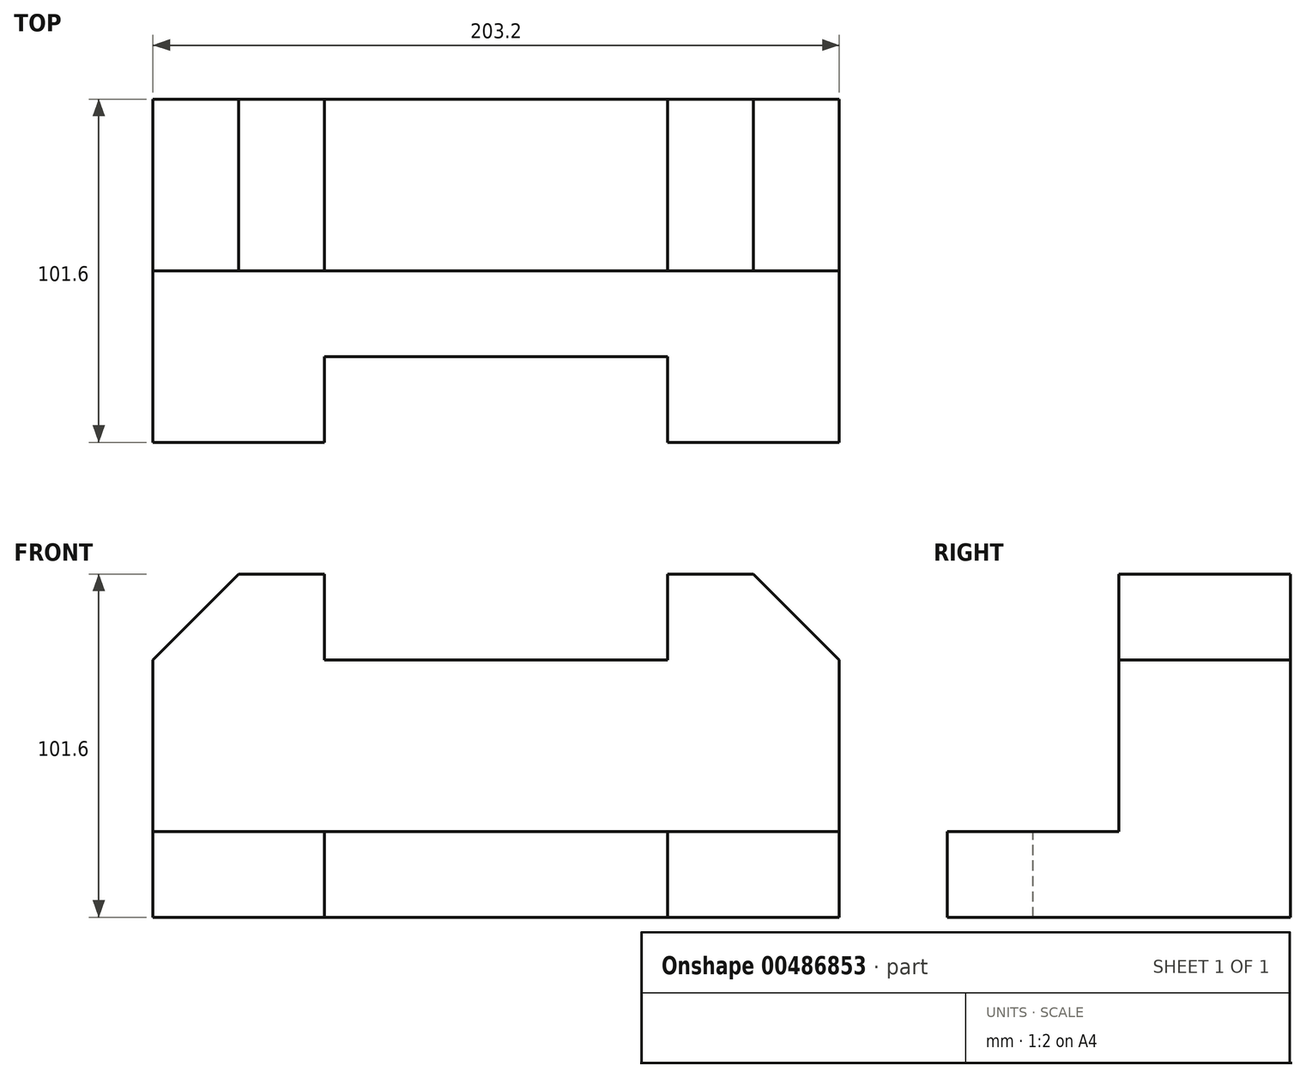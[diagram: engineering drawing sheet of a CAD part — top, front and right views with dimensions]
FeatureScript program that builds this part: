
annotation { "Feature Type Name" : "Feature", "Feature Type Description" : "" }
export const myFeature = defineFeature(function(context is Context, id is Id, definition is map)
    precondition{}
    {
        {
            var Q0;
            Q0=qCreatedBy(makeId("Top.planeOp"),FACE);
            var sketch = newSketch(context, id + "F0", { "sketchPlane" : qUnion([Q0])});
            skLineSegment(sketch, "E0.bottom", {"start": v(158.57, -5.99) * mm, "end": v(-44.63, -5.99) * mm});
            skLineSegment(sketch, "E0.top", {"start": v(158.57, 44.81) * mm, "end": v(-44.63, 44.81) * mm});
            skLineSegment(sketch, "E0.left", {"start": v(158.57, -5.99) * mm, "end": v(158.57, 44.81) * mm});
            skLineSegment(sketch, "E0.right", {"start": v(-44.63, -5.99) * mm, "end": v(-44.63, 44.81) * mm});
            skSolve(sketch);
        }
        {
            var Q0;
            Q0 = qSketchRegion(id + "F0", true);
            extrude(context, id + "F1", {"entities" : qUnion([Q0]), "depth" : 25.4 * mm});
        }
        {
            var Q0;
            Q0=makeQuery(id+"F1.opExtrude","SWEPT_FACE",FACE,{"disambiguationData":[OSD([sQuery(id+"F0.wireOp",EDGE,"E0.bottom")])]});
            var sketch = newSketch(context, id + "F2", { "sketchPlane" : qUnion([Q0])});
            skLineSegment(sketch, "E1.right", {"start": v(6.17, 0) * mm, "end": v(6.17, 25.4) * mm});
            skLineSegment(sketch, "E2.bottom", {"start": v(6.17, 0) * mm, "end": v(107.77, 0) * mm});
            skLineSegment(sketch, "E2.top", {"start": v(6.17, 25.4) * mm, "end": v(107.77, 25.4) * mm});
            skLineSegment(sketch, "E2.right", {"start": v(107.77, 0) * mm, "end": v(107.77, 25.4) * mm});
            skSolve(sketch);
        }
        {
            var Q0;
            Q0 = qSketchRegion(id + "F2", true);
            extrude(context, id + "F3", {"entities" : qUnion([Q0]), "operationType" : NewBodyOperationType.REMOVE, "oppositeDirection" : true, "depth" : 25.4 * mm});
        }
        {
            var Q0;
            Q0=makeQuery(id+"F1.opExtrude","SWEPT_FACE",FACE,{"disambiguationData":[OSD([sQuery(id+"F0.wireOp",EDGE,"E0.top")])]});
            var sketch = newSketch(context, id + "F4", { "sketchPlane" : qUnion([Q0])});
            skLineSegment(sketch, "E3.bottom", {"start": v(44.63, 0) * mm, "end": v(-158.57, 0) * mm});
            skLineSegment(sketch, "E3.top", {"start": v(44.63, 76.2) * mm, "end": v(-158.57, 76.2) * mm});
            skLineSegment(sketch, "E3.left", {"start": v(44.63, 0) * mm, "end": v(44.63, 76.2) * mm});
            skLineSegment(sketch, "E3.right", {"start": v(-158.57, 0) * mm, "end": v(-158.57, 76.2) * mm});
            skSolve(sketch);
        }
        {
            var Q0;
            Q0 = qSketchRegion(id + "F4", true);
            extrude(context, id + "F5", {"entities" : qUnion([Q0]), "operationType" : NewBodyOperationType.ADD, "depth" : 50.8 * mm});
        }
        {
            var Q0;
            Q0=makeQuery(id+"F5.opExtrude","CAP_FACE",FACE,{"disambiguationData":[OSD([sQuery(id+"F4.wireOp",EDGE,"E3.bottom"),sQuery(id+"F4.wireOp",EDGE,"E3.top"),sQuery(id+"F4.wireOp",EDGE,"E3.left"),sQuery(id+"F4.wireOp",EDGE,"E3.right")])],"isStart":true});
            var sketch = newSketch(context, id + "F6", { "sketchPlane" : qUnion([Q0])});
            skLineSegment(sketch, "E4.bottom", {"start": v(158.57, 76.2) * mm, "end": v(107.77, 76.2) * mm});
            skLineSegment(sketch, "E4.top", {"start": v(133.17, 101.6) * mm, "end": v(107.77, 101.6) * mm});
            skLineSegment(sketch, "E4.right", {"start": v(107.77, 76.2) * mm, "end": v(107.77, 101.6) * mm});
            skLineSegment(sketch, "E5", {"start": v(133.17, 101.6) * mm, "end": v(158.57, 76.2) * mm});
            skPoint(sketch, "E6.orphan", {"position": v(158.57, 101.6) * mm});
            skSolve(sketch);
        }
        {
            var Q0;
            Q0 = qSketchRegion(id + "F6", true);
            extrude(context, id + "F7", {"entities" : qUnion([Q0]), "operationType" : NewBodyOperationType.ADD, "oppositeDirection" : true, "depth" : 50.8 * mm});
        }
        {
            var Q0;
            Q0=makeQuery(id+"F7.boolean.opBoolean","MERGE",FACE,{"derivedFrom":[makeQuery(id+"F5.opExtrude","CAP_FACE",FACE,{"disambiguationData":[OSD([sQuery(id+"F4.wireOp",EDGE,"E3.bottom"),sQuery(id+"F4.wireOp",EDGE,"E3.top"),sQuery(id+"F4.wireOp",EDGE,"E3.left"),sQuery(id+"F4.wireOp",EDGE,"E3.right")])],"isStart":true}),makeQuery(id+"F7.opExtrude","CAP_FACE",FACE,{"disambiguationData":[OSD([sQuery(id+"F6.wireOp",EDGE,"E4.bottom"),sQuery(id+"F6.wireOp",EDGE,"E4.top"),sQuery(id+"F6.wireOp",EDGE,"E4.right"),sQuery(id+"F6.wireOp",EDGE,"E5")])],"isStart":true})]});
            var sketch = newSketch(context, id + "F8", { "sketchPlane" : qUnion([Q0])});
            skLineSegment(sketch, "E7.bottom", {"start": v(-44.63, 76.2) * mm, "end": v(6.17, 76.2) * mm});
            skLineSegment(sketch, "E7.top", {"start": v(-19.23, 101.6) * mm, "end": v(6.17, 101.6) * mm});
            skLineSegment(sketch, "E7.right", {"start": v(6.17, 76.2) * mm, "end": v(6.17, 101.6) * mm});
            skLineSegment(sketch, "E8", {"start": v(-19.23, 101.6) * mm, "end": v(-44.63, 76.2) * mm});
            skPoint(sketch, "E9.orphan", {"position": v(-44.63, 101.6) * mm});
            skSolve(sketch);
        }
        {
            var Q0;
            Q0 = qSketchRegion(id + "F8", true);
            extrude(context, id + "F9", {"entities" : qUnion([Q0]), "operationType" : NewBodyOperationType.ADD, "oppositeDirection" : true, "depth" : 50.8 * mm});
        }
    });
